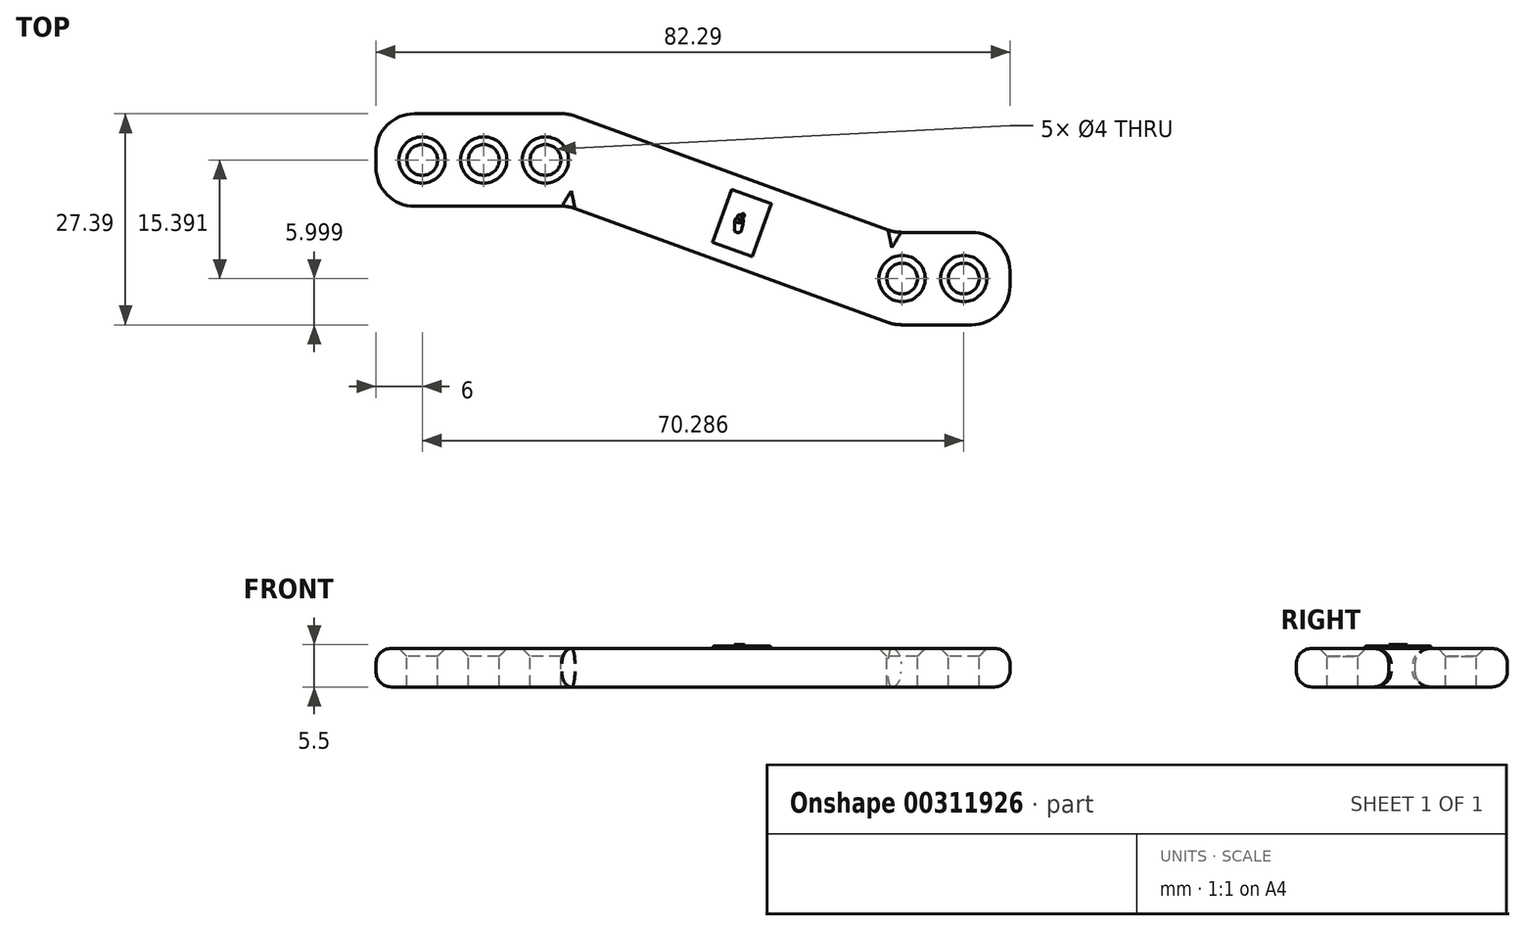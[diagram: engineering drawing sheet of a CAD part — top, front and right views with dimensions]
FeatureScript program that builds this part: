
annotation { "Feature Type Name" : "Feature", "Feature Type Description" : "" }
export const myFeature = defineFeature(function(context is Context, id is Id, definition is map)
    precondition{}
    {
        {
            var Q0;
            Q0=qCreatedBy(makeId("Top.planeOp"),FACE);
            var sketch = newSketch(context, id + "F0", { "sketchPlane" : qUnion([Q0])});
            skLineSegment(sketch, "E0.bottom", {"start": v(0, 12) * mm, "end": v(25, 12) * mm});
            skLineSegment(sketch, "E0.top", {"start": v(0, 0) * mm, "end": v(25, 0) * mm});
            skLineSegment(sketch, "E0.left", {"start": v(0, 12) * mm, "end": v(0, 0) * mm});
            skLineSegment(sketch, "E0.right", {"start": v(25, 12) * mm, "end": v(25, 0) * mm});
            skLineSegment(sketch, "E1.bottom", {"start": v(67.29, -3.4) * mm, "end": v(82.29, -3.4) * mm});
            skLineSegment(sketch, "E1.top", {"start": v(67.29, -15.4) * mm, "end": v(82.29, -15.4) * mm});
            skLineSegment(sketch, "E1.left", {"start": v(67.29, -3.4) * mm, "end": v(67.29, -15.4) * mm});
            skLineSegment(sketch, "E1.right", {"start": v(82.29, -3.4) * mm, "end": v(82.29, -15.4) * mm});
            skLineSegment(sketch, "E2", {"start": v(25, 12) * mm, "end": v(67.29, -3.4) * mm});
            skLineSegment(sketch, "E3", {"start": v(67.29, -15.4) * mm, "end": v(25, 0) * mm});
            skSolve(sketch);
        }
        {
            var Q0;
            Q0=makeQuery(id+"F0.imprint","IMPRINT",FACE,{"disambiguationData":[TD([[makeQuery(id+"F0.imprint","IMPRINT",EDGE,{"derivedFrom":sQuery(id+"F0.wireOp",EDGE,"E0.right")}),1.0]])]});
            var Q1;
            Q1=makeQuery(id+"F0.imprint","IMPRINT",FACE,{"disambiguationData":[TD([[makeQuery(id+"F0.imprint","IMPRINT",EDGE,{"derivedFrom":sQuery(id+"F0.wireOp",EDGE,"E1.bottom")}),-1.0]])]});
            var Q2;
            Q2=makeQuery(id+"F0.imprint","IMPRINT",FACE,{"disambiguationData":[TD([[makeQuery(id+"F0.imprint","IMPRINT",EDGE,{"derivedFrom":sQuery(id+"F0.wireOp",EDGE,"E0.bottom")}),-1.0]])]});
            extrude(context, id + "F1", {"entities" : qUnion([Q0, Q1, Q2]), "depth" : 5 * mm});
        }
        {
            var Q0;
            Q0=makeQuery(id+"F1.opExtrude","CAP_FACE",FACE,{"disambiguationData":[OSD([sQuery(id+"F0.wireOp",EDGE,"E0.bottom"),sQuery(id+"F0.wireOp",EDGE,"E0.top"),sQuery(id+"F0.wireOp",EDGE,"E0.left"),sQuery(id+"F0.wireOp",EDGE,"E1.bottom"),sQuery(id+"F0.wireOp",EDGE,"E1.top"),sQuery(id+"F0.wireOp",EDGE,"E1.right"),sQuery(id+"F0.wireOp",EDGE,"E2"),sQuery(id+"F0.wireOp",EDGE,"E3")])],"isStart":false});
            var sketch = newSketch(context, id + "F2", { "sketchPlane" : qUnion([Q0])});
            skCircle(sketch, "E4", {"center": v(6, 6) * mm, "radius": 2 * mm});
            skCircle(sketch, "E5", {"center": v(76.29, -9.4) * mm, "radius": 2 * mm});
            skCircle(sketch, "E6.1.0.0", {"center": v(14, 6) * mm, "radius": 2 * mm});
            skCircle(sketch, "E6.2.0.0", {"center": v(22, 6) * mm, "radius": 2 * mm});
            skLineSegment(sketch, "E6.direction1", {"start": v(6, 6) * mm, "end": v(14, 6) * mm, "construction": true});
            skCircle(sketch, "E7.1.0.0", {"center": v(68.29, -9.4) * mm, "radius": 2 * mm});
            skLineSegment(sketch, "E7.direction1", {"start": v(76.29, -9.4) * mm, "end": v(68.29, -9.4) * mm, "construction": true});
            skSolve(sketch);
        }
        {
            var Q0;
            Q0 = qSketchRegion(id + "F2", true);
            extrude(context, id + "F3", {"entities" : qUnion([Q0]), "operationType" : NewBodyOperationType.REMOVE, "endBound" : BoundingType.THROUGH_ALL, "oppositeDirection" : true, "depth" : 25 * mm});
        }
        {
            var Q0;
            Q0=makeQuery(id+"F1.opExtrude","CAP_EDGE",EDGE,{"disambiguationData":[OSD([sQuery(id+"F0.wireOp",EDGE,"E0.top")])],"isStart":false});
            var Q1;
            Q1=makeQuery(id+"F1.opExtrude","CAP_EDGE",EDGE,{"disambiguationData":[OSD([sQuery(id+"F0.wireOp",EDGE,"E3")])],"isStart":false});
            var Q2;
            Q2=makeQuery(id+"F1.opExtrude","CAP_EDGE",EDGE,{"disambiguationData":[OSD([sQuery(id+"F0.wireOp",EDGE,"E1.right")])],"isStart":false});
            var Q3;
            Q3=makeQuery(id+"F1.opExtrude","CAP_EDGE",EDGE,{"disambiguationData":[OSD([sQuery(id+"F0.wireOp",EDGE,"E1.bottom")])],"isStart":false});
            var Q4;
            Q4=makeQuery(id+"F1.opExtrude","CAP_EDGE",EDGE,{"disambiguationData":[OSD([sQuery(id+"F0.wireOp",EDGE,"E2")])],"isStart":false});
            var Q5;
            Q5=makeQuery(id+"F1.opExtrude","CAP_EDGE",EDGE,{"disambiguationData":[OSD([sQuery(id+"F0.wireOp",EDGE,"E0.bottom")])],"isStart":false});
            var Q6;
            Q6=makeQuery(id+"F1.opExtrude","CAP_EDGE",EDGE,{"disambiguationData":[OSD([sQuery(id+"F0.wireOp",EDGE,"E0.left")])],"isStart":false});
            var Q7;
            Q7=makeQuery(id+"F1.opExtrude","CAP_EDGE",EDGE,{"disambiguationData":[OSD([sQuery(id+"F0.wireOp",EDGE,"E1.top")])],"isStart":false});
            var Q8;
            Q8=makeQuery(id+"F1.opExtrude","CAP_EDGE",EDGE,{"disambiguationData":[OSD([sQuery(id+"F0.wireOp",EDGE,"E0.top")])],"isStart":true});
            var Q9;
            Q9=makeQuery(id+"F1.opExtrude","CAP_EDGE",EDGE,{"disambiguationData":[OSD([sQuery(id+"F0.wireOp",EDGE,"E0.left")])],"isStart":true});
            var Q10;
            Q10=makeQuery(id+"F1.opExtrude","CAP_EDGE",EDGE,{"disambiguationData":[OSD([sQuery(id+"F0.wireOp",EDGE,"E0.bottom")])],"isStart":true});
            var Q11;
            Q11=makeQuery(id+"F1.opExtrude","CAP_EDGE",EDGE,{"disambiguationData":[OSD([sQuery(id+"F0.wireOp",EDGE,"E3")])],"isStart":true});
            var Q12;
            Q12=makeQuery(id+"F1.opExtrude","CAP_EDGE",EDGE,{"disambiguationData":[OSD([sQuery(id+"F0.wireOp",EDGE,"E1.top")])],"isStart":true});
            var Q13;
            Q13=makeQuery(id+"F1.opExtrude","CAP_EDGE",EDGE,{"disambiguationData":[OSD([sQuery(id+"F0.wireOp",EDGE,"E1.right")])],"isStart":true});
            var Q14;
            Q14=makeQuery(id+"F1.opExtrude","CAP_EDGE",EDGE,{"disambiguationData":[OSD([sQuery(id+"F0.wireOp",EDGE,"E2")])],"isStart":true});
            var Q15;
            Q15=makeQuery(id+"F1.opExtrude","CAP_EDGE",EDGE,{"disambiguationData":[OSD([sQuery(id+"F0.wireOp",EDGE,"E1.bottom")])],"isStart":true});
            fillet(context, id + "F4", {"entities" : qUnion([Q0, Q1, Q2, Q3, Q4, Q5, Q6, Q7, Q8, Q9, Q10, Q11, Q12, Q13, Q14, Q15]), "radius" : 2 * mm, "tangentPropagation" : true, "allowEdgeOverflow" : false});
        }
        {
            var Q0;
            Q0=makeQuery(id+"F1.opExtrude","SWEPT_EDGE",EDGE,{"disambiguationData":[OSD([sQuery(id+"F0.wireOp",EDGE,"E0.top"),sQuery(id+"F0.wireOp",EDGE,"E0.left")])]});
            var Q1;
            Q1=makeQuery(id+"F1.opExtrude","SWEPT_EDGE",EDGE,{"disambiguationData":[OSD([sQuery(id+"F0.wireOp",EDGE,"E0.top"),sQuery(id+"F0.wireOp",EDGE,"E0.right"),sQuery(id+"F0.wireOp",EDGE,"E3")])]});
            var Q2;
            Q2=makeQuery(id+"F1.opExtrude","SWEPT_EDGE",EDGE,{"disambiguationData":[OSD([sQuery(id+"F0.wireOp",EDGE,"E1.top"),sQuery(id+"F0.wireOp",EDGE,"E1.left"),sQuery(id+"F0.wireOp",EDGE,"E3")])]});
            var Q3;
            Q3=makeQuery(id+"F1.opExtrude","SWEPT_EDGE",EDGE,{"disambiguationData":[OSD([sQuery(id+"F0.wireOp",EDGE,"E1.top"),sQuery(id+"F0.wireOp",EDGE,"E1.right")])]});
            var Q4;
            Q4=makeQuery(id+"F1.opExtrude","SWEPT_EDGE",EDGE,{"disambiguationData":[OSD([sQuery(id+"F0.wireOp",EDGE,"E1.bottom"),sQuery(id+"F0.wireOp",EDGE,"E1.right")])]});
            var Q5;
            Q5=makeQuery(id+"F1.opExtrude","SWEPT_EDGE",EDGE,{"disambiguationData":[OSD([sQuery(id+"F0.wireOp",EDGE,"E1.bottom"),sQuery(id+"F0.wireOp",EDGE,"E1.left"),sQuery(id+"F0.wireOp",EDGE,"E2")])]});
            var Q6;
            Q6=makeQuery(id+"F1.opExtrude","SWEPT_EDGE",EDGE,{"disambiguationData":[OSD([sQuery(id+"F0.wireOp",EDGE,"E0.bottom"),sQuery(id+"F0.wireOp",EDGE,"E0.right"),sQuery(id+"F0.wireOp",EDGE,"E2")])]});
            var Q7;
            Q7=makeQuery(id+"F1.opExtrude","SWEPT_EDGE",EDGE,{"disambiguationData":[OSD([sQuery(id+"F0.wireOp",EDGE,"E0.bottom"),sQuery(id+"F0.wireOp",EDGE,"E0.left")])]});
            fillet(context, id + "F5", {"entities" : qUnion([Q0, Q1, Q2, Q3, Q4, Q5, Q6, Q7]), "radius" : 5 * mm, "tangentPropagation" : true, "allowEdgeOverflow" : false});
        }
        {
            var Q0;
            Q0=makeQuery(id+"F1.opExtrude","CAP_FACE",FACE,{"disambiguationData":[OSD([sQuery(id+"F0.wireOp",EDGE,"E0.bottom"),sQuery(id+"F0.wireOp",EDGE,"E0.top"),sQuery(id+"F0.wireOp",EDGE,"E0.left"),sQuery(id+"F0.wireOp",EDGE,"E1.bottom"),sQuery(id+"F0.wireOp",EDGE,"E1.top"),sQuery(id+"F0.wireOp",EDGE,"E1.right"),sQuery(id+"F0.wireOp",EDGE,"E2"),sQuery(id+"F0.wireOp",EDGE,"E3")])],"isStart":false});
            chamfer(context, id + "F6", {"entities" : qUnion([Q0]), "width" : 1 * mm, "tangentPropagation" : true});
        }
        {
            var Q0;
            Q0=makeQuery(id+"F1.opExtrude","CAP_FACE",FACE,{"disambiguationData":[OSD([sQuery(id+"F0.wireOp",EDGE,"E0.bottom"),sQuery(id+"F0.wireOp",EDGE,"E0.top"),sQuery(id+"F0.wireOp",EDGE,"E0.left"),sQuery(id+"F0.wireOp",EDGE,"E1.bottom"),sQuery(id+"F0.wireOp",EDGE,"E1.top"),sQuery(id+"F0.wireOp",EDGE,"E1.right"),sQuery(id+"F0.wireOp",EDGE,"E2"),sQuery(id+"F0.wireOp",EDGE,"E3")])],"isStart":false});
            var sketch = newSketch(context, id + "F7", { "sketchPlane" : qUnion([Q0])});
            skPoint(sketch, "E8", {"position": v(46.25, -5.6) * mm});
            skFitSpline(sketch, "E9", {"points": [v(46.95, -1.24) * mm, v(47, -1.17) * mm, v(47.1, -1.13) * mm, v(47.23, -1.13) * mm, v(47.31, -1.14) * mm, v(47.52, -1.02) * mm, v(47.7, -0.97) * mm, v(47.8, -1.06) * mm, v(47.83, -1.12) * mm, v(47.82, -1.28) * mm, v(47.64, -1.5) * mm, v(47.48, -1.6) * mm], "startDerivative": vector(0.57, 1.1) * mm, "endDerivative": vector(-1.49, -0.68) * mm});
            skFitSpline(sketch, "E10", {"points": [v(46.95, -1.24) * mm, v(46.91, -1.5) * mm], "startDerivative": vector(-0.03, -0.27) * mm, "endDerivative": vector(-0.03, -0.27) * mm});
            skFitSpline(sketch, "E11", {"points": [v(47.41, -1.2) * mm, v(47.56, -1.1) * mm, v(47.67, -1.06) * mm, v(47.74, -1.06) * mm, v(47.72, -1.24) * mm, v(47.64, -1.39) * mm, v(47.45, -1.5) * mm], "startDerivative": vector(0.83, 0.61) * mm, "endDerivative": vector(-1.06, -0.54) * mm});
            skFitSpline(sketch, "E12", {"points": [v(47.41, -1.2) * mm, v(47.46, -1.27) * mm, v(47.46, -1.33) * mm, v(47.45, -1.5) * mm], "startDerivative": vector(0.22, -0.2) * mm, "endDerivative": vector(-0.03, -0.44) * mm});
            skFitSpline(sketch, "E13", {"points": [v(46.91, -1.5) * mm, v(46.82, -1.53) * mm, v(46.69, -1.62) * mm, v(46.6, -1.77) * mm, v(46.58, -1.85) * mm, v(46.51, -3.05) * mm, v(46.5, -3.07) * mm, v(46.5, -3.07) * mm], "startDerivative": vector(-0.75, -0.2) * mm, "endDerivative": vector(-0.16, 0.16) * mm});
            skFitSpline(sketch, "E14", {"points": [v(47.48, -1.6) * mm, v(47.64, -1.72) * mm, v(47.7, -1.95) * mm], "startDerivative": vector(0.37, -0.21) * mm, "endDerivative": vector(0.06, -0.49) * mm});
            skFitSpline(sketch, "E15", {"points": [v(47.7, -1.95) * mm, v(47.45, -3.12) * mm, v(47.45, -3.16) * mm, v(47.38, -3.26) * mm, v(47.22, -3.38) * mm, v(46.9, -3.42) * mm, v(46.62, -3.28) * mm, v(46.5, -3.07) * mm], "startDerivative": vector(-1.2, -5.4) * mm, "endDerivative": vector(-0.68, 1.7) * mm});
            skFitSpline(sketch, "E16", {"points": [v(46.88, -1.51) * mm, v(46.91, -1.6) * mm, v(46.98, -1.68) * mm, v(47.1, -1.73) * mm, v(47.3, -1.73) * mm, v(47.43, -1.66) * mm, v(47.48, -1.6) * mm], "startDerivative": vector(0.15, -0.58) * mm, "endDerivative": vector(0.32, 0.45) * mm});
            skFitSpline(sketch, "E17", {"points": [v(46.6, -1.77) * mm, v(46.6, -1.88) * mm, v(46.7, -2.01) * mm, v(46.91, -2.13) * mm, v(47.13, -2.17) * mm, v(47.45, -2.15) * mm, v(47.63, -2.03) * mm, v(47.69, -1.86) * mm], "startDerivative": vector(-0.15, -1.04) * mm, "endDerivative": vector(0.23, 1.36) * mm});
            skLineSegment(sketch, "E18", {"start": v(43.68, -4.67) * mm, "end": v(46.17, 2.17) * mm});
            skLineSegment(sketch, "E19", {"start": v(51.3, 0.3) * mm, "end": v(48.81, -6.54) * mm});
            skLineSegment(sketch, "E20", {"start": v(43.68, -4.67) * mm, "end": v(48.81, -6.54) * mm});
            skLineSegment(sketch, "E21", {"start": v(46.17, 2.17) * mm, "end": v(51.3, 0.3) * mm});
            skSolve(sketch);
        }
        {
            var Q0;
            {var subQ1=sQuery(id+"F7.wireOp",EDGE,"E9");Q0=makeQuery(id+"F7.imprint","IMPRINT",FACE,{"disambiguationData":[TD([[makeQuery(id+"F7.imprint","IMPRINT",EDGE,{"derivedFrom":subQ1}),-1.0]])]});}
            var Q1;
            {var subQ0=sQuery(id+"F7.wireOp",EDGE,"E15");Q1=makeQuery(id+"F7.imprint","IMPRINT",FACE,{"disambiguationData":[TD([[makeQuery(id+"F7.imprint","IMPRINT",EDGE,{"derivedFrom":subQ0}),-1.0]])]});}
            extrude(context, id + "F8", {"entities" : qUnion([Q0, Q1]), "operationType" : NewBodyOperationType.ADD, "depth" : .5 * mm});
        }
        {
            var Q0;
            Q0 = qSketchRegion(id + "F7", true);
            extrude(context, id + "F9", {"entities" : qUnion([Q0]), "operationType" : NewBodyOperationType.ADD, "depth" : 0.3 * mm});
        }
        {
            var Q0;
            Q0=makeQuery(id+"F9.opExtrude","CAP_EDGE",EDGE,{"disambiguationData":[OSD([sQuery(id+"F7.wireOp",EDGE,"E20")])],"isStart":false});
            var Q1;
            Q1=makeQuery(id+"F9.opExtrude","CAP_EDGE",EDGE,{"disambiguationData":[OSD([sQuery(id+"F7.wireOp",EDGE,"E19")])],"isStart":false});
            var Q2;
            Q2=makeQuery(id+"F9.opExtrude","CAP_EDGE",EDGE,{"disambiguationData":[OSD([sQuery(id+"F7.wireOp",EDGE,"E18")])],"isStart":false});
            var Q3;
            Q3=makeQuery(id+"F9.opExtrude","CAP_EDGE",EDGE,{"disambiguationData":[OSD([sQuery(id+"F7.wireOp",EDGE,"E21")])],"isStart":false});
            fillet(context, id + "F10", {"entities" : qUnion([Q0, Q1, Q2, Q3]), "radius" : .2 * mm, "tangentPropagation" : true, "allowEdgeOverflow" : false});
        }
    });
